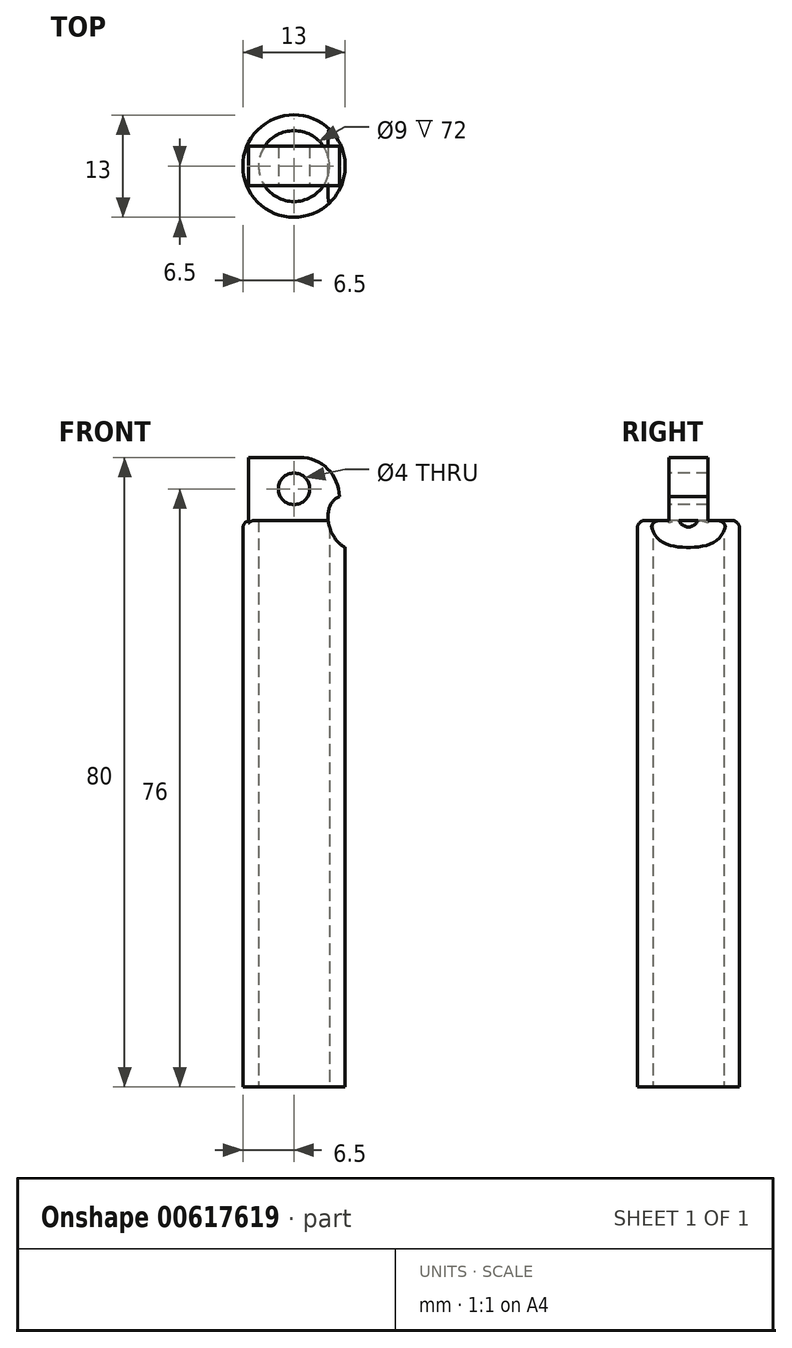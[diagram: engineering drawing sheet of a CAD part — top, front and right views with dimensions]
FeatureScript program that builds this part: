
annotation { "Feature Type Name" : "Feature", "Feature Type Description" : "" }
export const myFeature = defineFeature(function(context is Context, id is Id, definition is map)
    precondition{}
    {
        {
            var Q0;
            Q0=qCreatedBy(makeId("Top.planeOp"),FACE);
            var sketch = newSketch(context, id + "F0", { "sketchPlane" : qUnion([Q0])});
            skCircle(sketch, "E0", {"center": v(0, 0) * mm, "radius": 6.5 * mm});
            skSolve(sketch);
        }
        {
            var Q0;
            Q0 = qSketchRegion(id + "F0", true);
            extrude(context, id + "F1", {"entities" : qUnion([Q0]), "depth" : 72 * mm, "offsetDistance" : 25 * mm});
        }
        {
            var Q0;
            Q0=makeQuery(id+"F1.opExtrude","CAP_FACE",FACE,{"disambiguationData":[OSD([sQuery(id+"F0.wireOp",EDGE,"E0")])],"isStart":false});
            var sketch = newSketch(context, id + "F2", { "sketchPlane" : qUnion([Q0])});
            skLineSegment(sketch, "E1.bottom", {"start": v(5.75, 2.5) * mm, "end": v(-5.75, 2.5) * mm});
            skLineSegment(sketch, "E1.top", {"start": v(5.75, -2.5) * mm, "end": v(-5.75, -2.5) * mm});
            skLineSegment(sketch, "E1.left", {"start": v(5.75, 2.5) * mm, "end": v(5.75, -2.5) * mm});
            skLineSegment(sketch, "E1.right", {"start": v(-5.75, 2.5) * mm, "end": v(-5.75, -2.5) * mm});
            skPoint(sketch, "E1.middle", {"position": v(0, 0) * mm});
            skSolve(sketch);
        }
        {
            var Q0;
            Q0=makeQuery(id+"F1.opExtrude","CAP_FACE",FACE,{"disambiguationData":[OSD([sQuery(id+"F0.wireOp",EDGE,"E0")])],"isStart":true});
            var Q1;
            Q1=makeQuery(id+"F1.opExtrude","CAP_FACE",FACE,{"disambiguationData":[OSD([sQuery(id+"F0.wireOp",EDGE,"E0")])],"isStart":false});
            shell(context, id + "F3", {"entities" : qUnion([Q0, Q1]), "thickness" : 2 * mm});
        }
        {
            var Q0;
            {var subQ1=makeQuery(id+"F1.opExtrude","CAP_EDGE",EDGE,{"disambiguationData":[OSD([sQuery(id+"F0.wireOp",EDGE,"E0")])],"isStart":false});var subQ10=sQuery(id+"F2.wireOp",EDGE,"E1.bottom");var subQ11=makeQuery(id+"F2.imprint","INTERSECT",VERTEX,{"disambiguationData":[OD(0.0)],"derivedFrom":[subQ1,subQ10]});Q0=makeQuery(id+"F2.imprint","IMPRINT",FACE,{"disambiguationData":[TD([[makeQuery(id+"F2.imprint","IMPRINT",EDGE,{"disambiguationData":[TD([[subQ11,-1.0]])],"derivedFrom":subQ10}),1.0]])]});}
            extrude(context, id + "F4", {"entities" : qUnion([Q0]), "operationType" : NewBodyOperationType.ADD, "depth" : 8 * mm, "offsetDistance" : 25 * mm});
        }
        {
            var Q0;
            Q0=makeQuery(id+"F4.opExtrude","SWEPT_FACE",FACE,{"disambiguationData":[OSD([sQuery(id+"F2.wireOp",EDGE,"E1.top")])]});
            var sketch = newSketch(context, id + "F5", { "sketchPlane" : qUnion([Q0])});
            skCircle(sketch, "E2", {"center": v(0, 76) * mm, "radius": 2 * mm});
            skPoint(sketch, "E2.centerSnap0", {"position": v(5.75, 76) * mm});
            skSolve(sketch);
        }
        {
            var Q0;
            Q0 = qSketchRegion(id + "F5", true);
            extrude(context, id + "F6", {"entities" : qUnion([Q0]), "operationType" : NewBodyOperationType.REMOVE, "oppositeDirection" : true, "depth" : 5 * mm, "offsetDistance" : 25 * mm});
        }
        {
            var Q0;
            Q0=makeQuery(id+"F4.opExtrude","CAP_EDGE",EDGE,{"disambiguationData":[OSD([sQuery(id+"F2.wireOp",EDGE,"E1.left")])],"isStart":false});
            fillet(context, id + "F7", {"entities" : qUnion([Q0]), "radius" : 5 * mm, "tangentPropagation" : true, "allowEdgeOverflow" : false});
        }
        {
            var Q0;
            {var subQ1=sQuery(id+"F0.wireOp",EDGE,"E0");var subQ2=makeQuery(id+"F1.opExtrude","CAP_EDGE",EDGE,{"disambiguationData":[OSD([subQ1])],"isStart":false});var subQ3=sQuery(id+"F2.wireOp",EDGE,"E1.left");Q0=makeQuery(id+"F4.boolean.opBoolean","SPLIT",EDGE,{"disambiguationData":[TD([makeQuery(id+"F4.opExtrude","SWEPT_FACE",FACE,{"disambiguationData":[OSD([subQ3])]})])],"derivedFrom":subQ2});}
            var Q1;
            {var subQ1=sQuery(id+"F0.wireOp",EDGE,"E0");var subQ2=makeQuery(id+"F1.opExtrude","CAP_EDGE",EDGE,{"disambiguationData":[OSD([subQ1])],"isStart":false});var subQ4=sQuery(id+"F2.wireOp",EDGE,"E1.top");Q1=makeQuery(id+"F4.boolean.opBoolean","SPLIT",EDGE,{"disambiguationData":[TD([makeQuery(id+"F4.opExtrude","SWEPT_FACE",FACE,{"disambiguationData":[OSD([subQ4])]})])],"derivedFrom":subQ2});}
            var Q2;
            {var subQ0=sQuery(id+"F2.wireOp",EDGE,"E1.bottom");var subQ1=sQuery(id+"F0.wireOp",EDGE,"E0");var subQ2=makeQuery(id+"F1.opExtrude","CAP_EDGE",EDGE,{"disambiguationData":[OSD([subQ1])],"isStart":false});Q2=makeQuery(id+"F4.boolean.opBoolean","SPLIT",EDGE,{"disambiguationData":[TD([makeQuery(id+"F4.opExtrude","SWEPT_FACE",FACE,{"disambiguationData":[OSD([subQ0])]})])],"derivedFrom":subQ2});}
            fillet(context, id + "F8", {"entities" : qUnion([Q0, Q1, Q2]), "radius" : 1 * mm, "tangentPropagation" : true, "allowEdgeOverflow" : false});
        }
        {
            var Q0;
            Q0=makeQuery(id+"F4.opExtrude","SWEPT_FACE",FACE,{"disambiguationData":[OSD([sQuery(id+"F2.wireOp",EDGE,"E1.top")])]});
            var sketch = newSketch(context, id + "F9", { "sketchPlane" : qUnion([Q0])});
            skEllipse(sketch, "E3", {"center": v(6.95, 71.71) * mm, "majorRadius": 3.5 * mm, "minorRadius": 2.5 * mm, "majorAxis": v(-0.34, 0.94)});
            skSolve(sketch);
        }
        {
            var Q0;
            Q0 = qSketchRegion(id + "F9", true);
            extrude(context, id + "F10", {"entities" : qUnion([Q0]), "operationType" : NewBodyOperationType.REMOVE, "depth" : 25 * mm, "offsetDistance" : 25 * mm, "hasSecondDirection" : true, "secondDirectionOppositeDirection" : true, "secondDirectionDepth" : 25 * mm});
        }
    });
